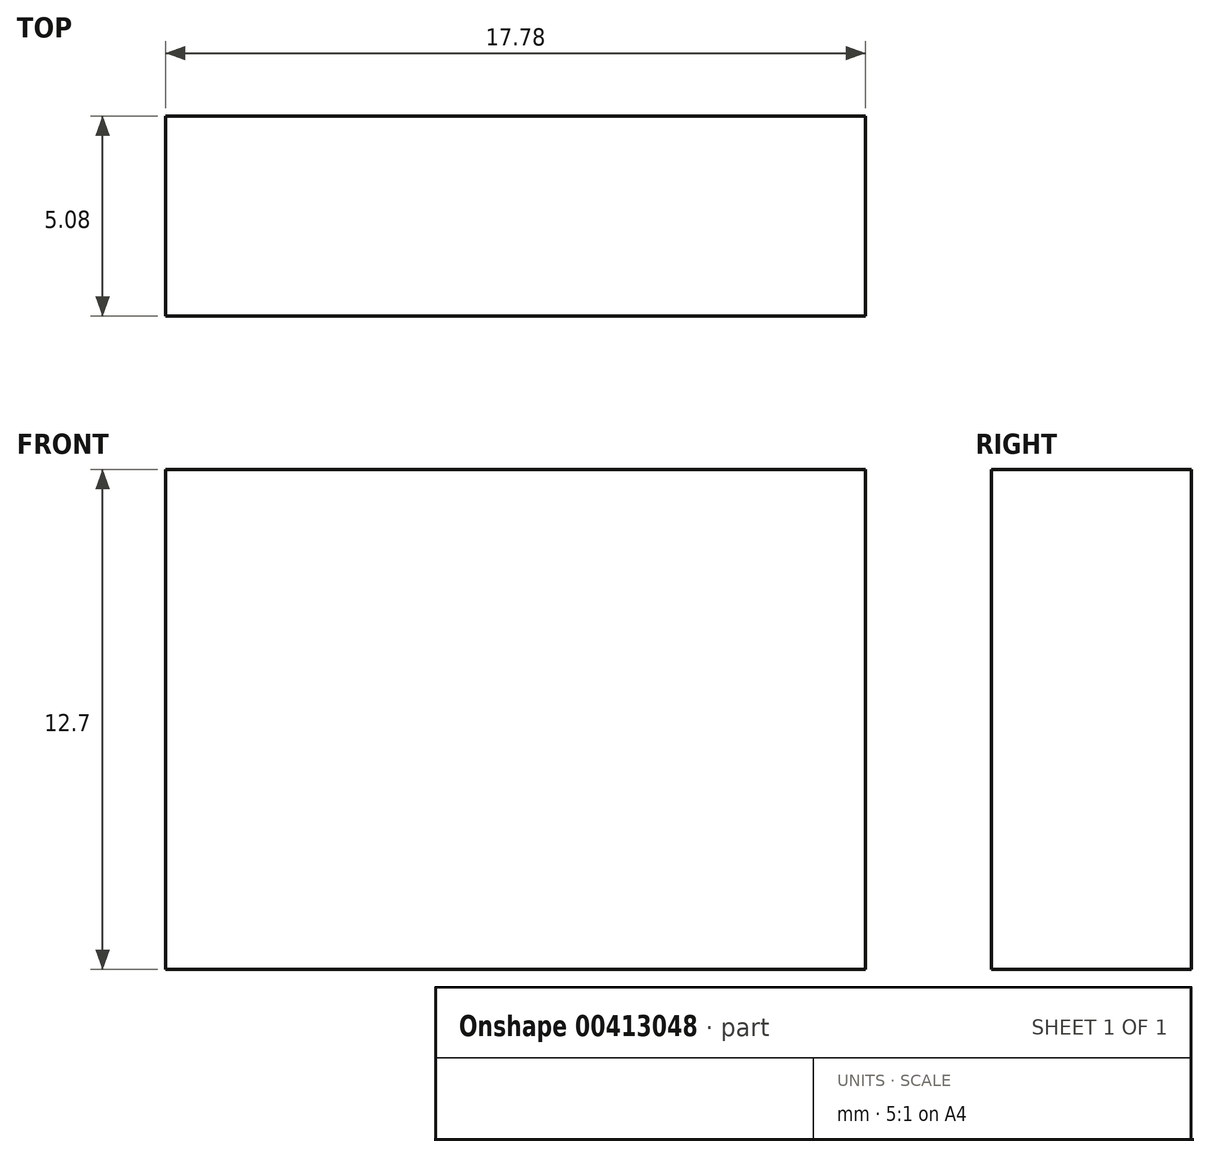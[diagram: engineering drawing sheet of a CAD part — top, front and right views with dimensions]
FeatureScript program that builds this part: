
annotation { "Feature Type Name" : "Feature", "Feature Type Description" : "" }
export const myFeature = defineFeature(function(context is Context, id is Id, definition is map)
    precondition{}
    {
        {
            var Q0;
            Q0=qCreatedBy(makeId("Front.planeOp"),FACE);
            var sketch = newSketch(context, id + "F0", { "sketchPlane" : qUnion([Q0])});
            skLineSegment(sketch, "E0.bottom", {"start": v(0, 0) * mm, "end": v(17.78, 0) * mm});
            skLineSegment(sketch, "E0.top", {"start": v(0, 12.7) * mm, "end": v(17.78, 12.7) * mm});
            skLineSegment(sketch, "E0.left", {"start": v(0, 0) * mm, "end": v(0, 12.7) * mm});
            skLineSegment(sketch, "E0.right", {"start": v(17.78, 0) * mm, "end": v(17.78, 12.7) * mm});
            skSolve(sketch);
        }
        {
            var Q0;
            Q0=makeQuery(id+"F0.imprint","IMPRINT",FACE,{"disambiguationData":[TD([[makeQuery(id+"F0.imprint","IMPRINT",EDGE,{"derivedFrom":sQuery(id+"F0.wireOp",EDGE,"E0.bottom")}),1.0]])]});
            extrude(context, id + "F1", {"entities" : qUnion([Q0]), "depth" : 5.08 * mm});
        }
    });
